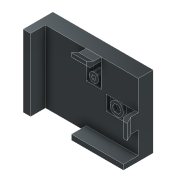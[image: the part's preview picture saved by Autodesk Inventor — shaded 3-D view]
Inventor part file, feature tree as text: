
AUTODESK INVENTOR PART (.ipt)
format: ipt  version: 2021 (Build 250183000, 183)  size: 377,344 bytes
history: native  units: in
note: dims shown in document units (in); Inventor stores cm internally (conversion verified against a paired STEP export)
features: extrude x30, sketch x30, projected_geometry x10
ambient origin geometry x8: Origin, YZ Plane, XZ Plane, XY Plane, X Axis, Y Axis, Z Axis, Center Point
bodies: Solid1 (feature_tree)
feature tree (70):
  extrude  "Extrusion1"  Depth=0.315in
  extrude  "Extrusion2"  Depth=0.5315in
  extrude  "Extrusion3"  Depth=0.5315in
  extrude  "Extrusion4"  Depth=0.0984in
  extrude  "Extrusion5"  Depth=0.0787in TaperAngle=0.0deg
  extrude  "Extrusion6"  Depth=0.2165in
  extrude  "Extrusion7"  Depth=0.0787in TaperAngle=0.0deg
  extrude  "Extrusion8"  Depth=0.0787in TaperAngle=0.0deg
  extrude  "Extrusion9"  Depth=0.0787in
  extrude  "Extrusion10"  Depth=0.0394in TaperAngle=0.0deg
  extrude  "Extrusion11"  Depth=0.0394in TaperAngle=0.0deg
  extrude  "Extrusion12"  Depth=0.0197in TaperAngle=0.0deg
  extrude  "Extrusion13"  Depth=0.0591in
  extrude  "Extrusion14"  Depth=0.0394in
  extrude  "Extrusion15"  Depth=0.1181in TaperAngle=0.0deg
  extrude  "Extrusion16"  Depth=0.1969in TaperAngle=0.0deg
  extrude  "Extrusion17"  Depth=0.0197in TaperAngle=0.0deg
  extrude  "Extrusion18"  Depth=0.0787in
  extrude  "Extrusion19"  Depth=0.0197in
  extrude  "Extrusion20"  Depth=0.0787in
  extrude  "Extrusion21"  Depth=0.0197in TaperAngle=0.0deg
  extrude  "Extrusion22"  Depth=0.0394in
  extrude  "Extrusion23"  Depth=0.1575in TaperAngle=0.0deg
  extrude  "Extrusion24"  Depth=0.0787in TaperAngle=0.0deg
  extrude  "Extrusion25"  Depth=0.0394in TaperAngle=0.0deg
  extrude  "Extrusion26"  Depth=0.0197in TaperAngle=0.0deg
  extrude  "Extrusion27"  [1 undecoded]
  extrude  "Extrusion28"  [1 undecoded]
  extrude  "Extrusion29"  [1 undecoded]
  extrude  "Extrusion30"  [1 undecoded]
  sketch  "Sketch1"  dims[d0=0.4528in d1=0.315in]
  sketch  "Sketch2"  dims[d2=0.5315in d3=0.4331in]
  sketch  "Sketch3"  dims[d4=0.0787in d5=0.0in d6=0.4528in d7=0.315in d8=0.5315in d9=0.4331in]
  sketch  "Sketch4"  dims[d10=0.0787in d11=0.0in d12=0.0984in]
  sketch  "Sketch5"  dims[d13=0.0984in d14=0.0787in d15=0.0in]
  sketch  "Sketch6"  dims[d16=0.2165in d17=0.2165in]
  sketch  "Sketch7"  dims[d18=0.0787in d19=0.0787in d20=0.0in]
  sketch  "Sketch8"  dims[d21=0.0787in d22=0.0in d23=0.0787in d24=0.0in]
  sketch  "Sketch9"  dims[d25=0.0787in d26=0.0in d28=0.1102in]
  sketch  "Sketch10"  dims[d29=0.0394in d30=0.0in d31=0.0394in d32=0.0in]
  sketch  "Sketch11"  dims[d33=0.0591in d34=0.0394in d35=0.0in]
  sketch  "Sketch12"  dims[d36=0.0197in d37=0.0in d38=0.0197in d39=0.0in]
  sketch  "Sketch13"  dims[d40=0.0394in d41=0.0591in]
  sketch  "Sketch14"  dims[d42=0.0197in d43=0.0in d44=0.0394in]
  sketch  "Sketch15"  dims[d45=0.1969in d46=0.0in d47=0.1181in d48=0.0in]
  projected_geometry  "Projected Loop1"
  sketch  "Sketch16"  dims[d49=0.1181in d50=0.0in d51=0.1969in d52=0.0in]
  projected_geometry  "Projected Loop2"
  sketch  "Sketch17"  dims[d53=0.0197in d54=0.0in d55=0.0197in d56=0.0in]
  projected_geometry  "Projected Loop3"
  sketch  "Sketch18"  dims[d57=0.1299in d58=0.0787in]
  projected_geometry  "Projected Loop4"
  sketch  "Sketch19"  dims[d59=0.0197in d60=0.0197in]
  projected_geometry  "Projected Loop5"
  sketch  "Sketch20"  dims[d61=0.1496in d62=0.0787in]
  sketch  "Sketch21"  dims[d63=0.0197in d64=0.0in d65=0.0197in d66=0.0in]
  sketch  "Sketch22"  dims[d67=0.0197in d68=0.0in d69=0.0394in]
  sketch  "Sketch23"  dims[d70=0.0197in d71=0.0in d72=0.1575in d73=0.0in]
  sketch  "Sketch24"  dims[d74=0.0787in d75=0.0in d76=0.0787in d77=0.0in]
  sketch  "Sketch25"  dims[d78=0.1575in d79=0.0in d80=0.0394in d81=0.0in]
  projected_geometry  "Projected Loop6"
  sketch  "Sketch26"  dims[d82=0.0197in d83=0.0in d84=0.0118in d85=0.0in]
  projected_geometry  "Projected Loop7"
  sketch  "Sketch27"  dims[d27=0.0197in]
  projected_geometry  "Projected Loop8"
  sketch  "Sketch28"
  sketch  "Sketch29"
  projected_geometry  "Projected Loop9"
  sketch  "Sketch30"
  projected_geometry  "Projected Loop10"
note: 4 required parameter values undecoded (feature->parameter linkage not recoverable at this tier; creation-order binding heuristic only, values carry confidence <= 0.55)
